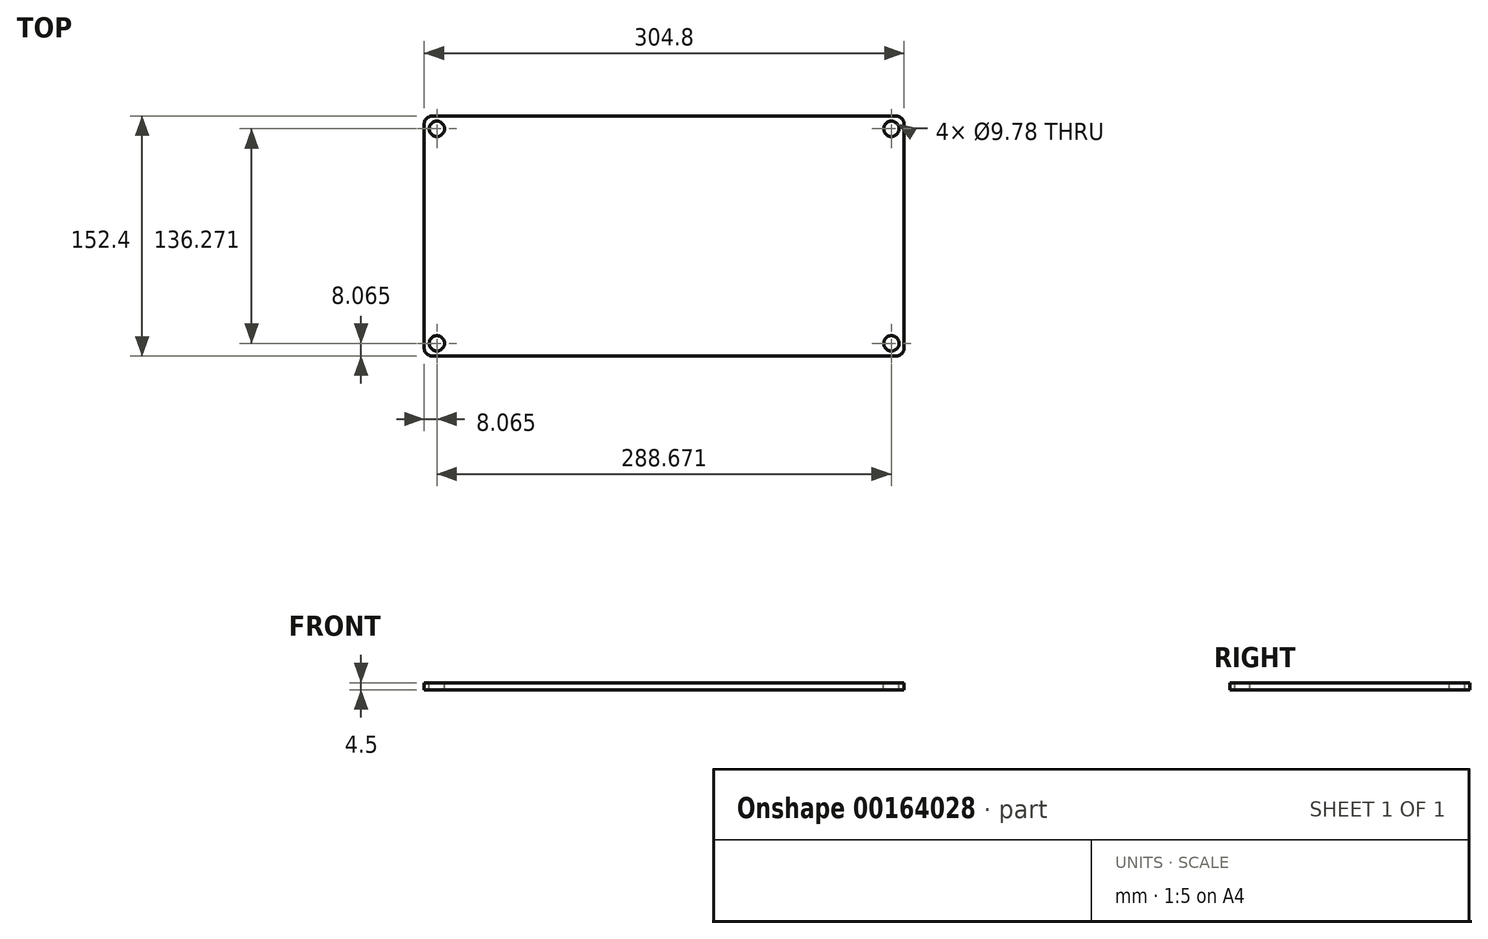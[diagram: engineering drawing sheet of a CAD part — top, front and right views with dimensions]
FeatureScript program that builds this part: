
annotation { "Feature Type Name" : "Feature", "Feature Type Description" : "" }
export const myFeature = defineFeature(function(context is Context, id is Id, definition is map)
    precondition{}
    {
        {
            var Q0;
            Q0=qCreatedBy(makeId("Top.planeOp"),FACE);
            var sketch = newSketch(context, id + "F0", { "sketchPlane" : qUnion([Q0])});
            skLineSegment(sketch, "E0.bottom", {"start": v(152.4, -76.2) * mm, "end": v(-152.4, -76.2) * mm});
            skLineSegment(sketch, "E0.top", {"start": v(152.4, 76.2) * mm, "end": v(-152.4, 76.2) * mm});
            skLineSegment(sketch, "E0.left", {"start": v(152.4, -76.2) * mm, "end": v(152.4, 76.2) * mm});
            skLineSegment(sketch, "E0.right", {"start": v(-152.4, -76.2) * mm, "end": v(-152.4, 76.2) * mm});
            skPoint(sketch, "E0.middle", {"position": v(0, 0) * mm});
            skSolve(sketch);
        }
        {
            var Q0;
            Q0=makeQuery(id+"F0.imprint","IMPRINT",FACE,{"disambiguationData":[TD([[makeQuery(id+"F0.imprint","IMPRINT",EDGE,{"derivedFrom":sQuery(id+"F0.wireOp",EDGE,"E0.bottom")}),-1.0]])]});
            extrude(context, id + "F1", {"entities" : qUnion([Q0]), "depth" : 4.5 * mm});
        }
        {
            var Q0;
            Q0=makeQuery(id+"F1.opExtrude","SWEPT_EDGE",EDGE,{"disambiguationData":[OSD([sQuery(id+"F0.wireOp",EDGE,"E0.top"),sQuery(id+"F0.wireOp",EDGE,"E0.right")])]});
            var Q1;
            Q1=makeQuery(id+"F1.opExtrude","SWEPT_EDGE",EDGE,{"disambiguationData":[OSD([sQuery(id+"F0.wireOp",EDGE,"E0.bottom"),sQuery(id+"F0.wireOp",EDGE,"E0.right")])]});
            var Q2;
            Q2=makeQuery(id+"F1.opExtrude","SWEPT_EDGE",EDGE,{"disambiguationData":[OSD([sQuery(id+"F0.wireOp",EDGE,"E0.bottom"),sQuery(id+"F0.wireOp",EDGE,"E0.left")])]});
            var Q3;
            Q3=makeQuery(id+"F1.opExtrude","SWEPT_EDGE",EDGE,{"disambiguationData":[OSD([sQuery(id+"F0.wireOp",EDGE,"E0.top"),sQuery(id+"F0.wireOp",EDGE,"E0.left")])]});
            fillet(context, id + "F2", {"entities" : qUnion([Q0, Q1, Q2, Q3]), "radius" : 5.08 * mm, "tangentPropagation" : true, "allowEdgeOverflow" : false});
        }
        {
            var Q0;
            Q0=makeQuery(id+"F1.opExtrude","CAP_FACE",FACE,{"disambiguationData":[OSD([sQuery(id+"F0.wireOp",EDGE,"E0.bottom"),sQuery(id+"F0.wireOp",EDGE,"E0.top"),sQuery(id+"F0.wireOp",EDGE,"E0.left"),sQuery(id+"F0.wireOp",EDGE,"E0.right")])],"isStart":false});
            var sketch = newSketch(context, id + "F3", { "sketchPlane" : qUnion([Q0])});
            skCircle(sketch, "E1", {"center": v(-144.34, 68.14) * mm, "radius": 4.89 * mm});
            skCircle(sketch, "E2", {"center": v(144.34, 68.14) * mm, "radius": 4.89 * mm});
            skCircle(sketch, "E3", {"center": v(144.34, -68.14) * mm, "radius": 4.89 * mm});
            skCircle(sketch, "E4", {"center": v(-144.34, -68.14) * mm, "radius": 4.89 * mm});
            skSolve(sketch);
        }
        {
            var Q0;
            Q0 = qSketchRegion(id + "F3", true);
            extrude(context, id + "F4", {"entities" : qUnion([Q0]), "operationType" : NewBodyOperationType.REMOVE, "endBound" : BoundingType.THROUGH_ALL, "oppositeDirection" : true, "depth" : 25.4 * mm});
        }
    });
